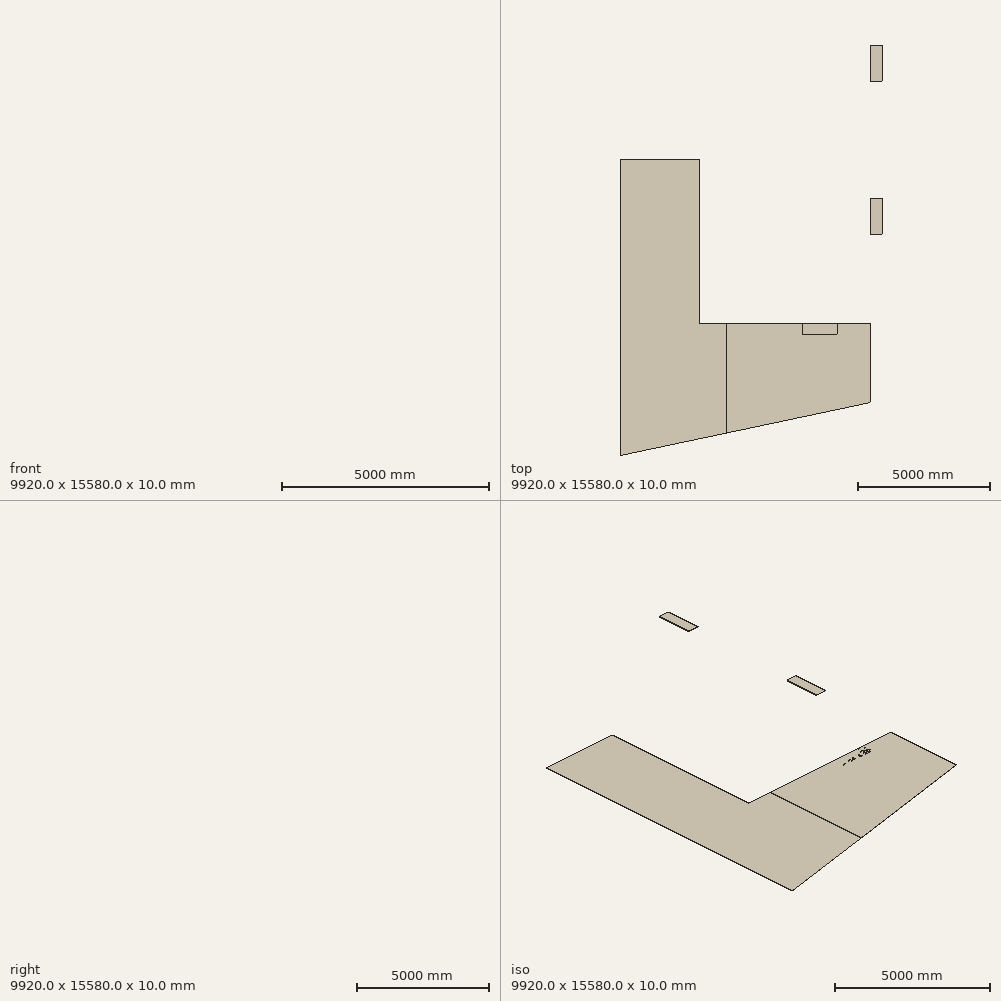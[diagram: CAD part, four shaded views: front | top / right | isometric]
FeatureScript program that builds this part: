
annotation { "Feature Type Name" : "Feature", "Feature Type Description" : "" }
export const myFeature = defineFeature(function(context is Context, id is Id, definition is map)
    precondition{}
    {
        {
            var Q0;
            Q0=qCreatedBy(makeId("Top.planeOp"),FACE);
            var sketch = newSketch(context, id + "F0", { "sketchPlane" : qUnion([Q0])});
            skLineSegment(sketch, "E0", {"start": v(0, 0) * mm, "end": v(14150, 3000) * mm});
            skLineSegment(sketch, "E1", {"start": v(14150, 3000) * mm, "end": v(14150, 27420) * mm});
            skLineSegment(sketch, "E2", {"start": v(14150, 27420) * mm, "end": v(0, 25000) * mm});
            skLineSegment(sketch, "E3", {"start": v(0, 25000) * mm, "end": v(0, 0) * mm});
            skSolve(sketch);
        }
        {
            var Q0;
            Q0=qCreatedBy(makeId("Top.planeOp"),FACE);
            var sketch = newSketch(context, id + "F1", { "sketchPlane" : qUnion([Q0])});
            skLineSegment(sketch, "E4.bottom", {"start": v(3000, 18250) * mm, "end": v(9500, 18250) * mm});
            skLineSegment(sketch, "E4.top", {"start": v(3000, 5000) * mm, "end": v(9500, 5000) * mm});
            skLineSegment(sketch, "E4.left", {"start": v(3000, 18250) * mm, "end": v(3000, 5000) * mm});
            skLineSegment(sketch, "E4.right", {"start": v(9500, 18250) * mm, "end": v(9500, 5000) * mm});
            skSolve(sketch);
        }
        {
            var Q0;
            Q0=qCreatedBy(makeId("Top.planeOp"),FACE);
            var sketch = newSketch(context, id + "F2", { "sketchPlane" : qUnion([Q0])});
            skLineSegment(sketch, "E5.bottom", {"start": v(3000, 11250) * mm, "end": v(0, 11250) * mm});
            skLineSegment(sketch, "E5.top", {"start": v(3000, 17250) * mm, "end": v(0, 17250) * mm});
            skLineSegment(sketch, "E5.left", {"start": v(3000, 11250) * mm, "end": v(3000, 17250) * mm});
            skLineSegment(sketch, "E5.right", {"start": v(0, 11250) * mm, "end": v(0, 17250) * mm});
            skSolve(sketch);
        }
        {
            var Q0;
            Q0=qCreatedBy(makeId("Top.planeOp"),FACE);
            var sketch = newSketch(context, id + "F3", { "sketchPlane" : qUnion([Q0])});
            skLineSegment(sketch, "E6", {"start": v(0, 11250) * mm, "end": v(3000, 11250) * mm});
            skLineSegment(sketch, "E7", {"start": v(3000, 11250) * mm, "end": v(3000, 5000) * mm});
            skLineSegment(sketch, "E8", {"start": v(3000, 5000) * mm, "end": v(4000, 5000) * mm});
            skLineSegment(sketch, "E9", {"start": v(4000, 5000) * mm, "end": v(4000, 848.06) * mm});
            skLineSegment(sketch, "E10", {"start": v(4000, 848.06) * mm, "end": v(0, 0) * mm});
            skLineSegment(sketch, "E11", {"start": v(0, 0) * mm, "end": v(0, 11250) * mm});
            skSolve(sketch);
        }
        {
            var Q0;
            Q0=qCreatedBy(makeId("Top.planeOp"),FACE);
            var sketch = newSketch(context, id + "F4", { "sketchPlane" : qUnion([Q0])});
            skLineSegment(sketch, "E12", {"start": v(4000, 4500) * mm, "end": v(10000, 4500) * mm});
            skLineSegment(sketch, "E13", {"start": v(10000, 4500) * mm, "end": v(10000, 18250) * mm});
            skLineSegment(sketch, "E14", {"start": v(10000, 18250) * mm, "end": v(9500, 18250) * mm});
            skLineSegment(sketch, "E15", {"start": v(9500, 18250) * mm, "end": v(9500, 5000) * mm});
            skLineSegment(sketch, "E16", {"start": v(9500, 5000) * mm, "end": v(4000, 5000) * mm});
            skLineSegment(sketch, "E17", {"start": v(4000, 5000) * mm, "end": v(4000, 4500) * mm});
            skSolve(sketch);
        }
        {
            var Q0;
            Q0=qCreatedBy(makeId("Top.planeOp"),FACE);
            var sketch = newSketch(context, id + "F5", { "sketchPlane" : qUnion([Q0])});
            skLineSegment(sketch, "E18.bottom", {"start": v(6880, 5000) * mm, "end": v(8230, 5000) * mm});
            skLineSegment(sketch, "E18.top", {"start": v(6880, 4580) * mm, "end": v(8230, 4580) * mm});
            skLineSegment(sketch, "E18.left", {"start": v(6880, 5000) * mm, "end": v(6880, 4580) * mm});
            skLineSegment(sketch, "E18.right", {"start": v(8230, 5000) * mm, "end": v(8230, 4580) * mm});
            skLineSegment(sketch, "E19.bottom", {"start": v(9500, 9750) * mm, "end": v(9920, 9750) * mm});
            skLineSegment(sketch, "E19.top", {"start": v(9500, 8400) * mm, "end": v(9920, 8400) * mm});
            skLineSegment(sketch, "E19.left", {"start": v(9500, 9750) * mm, "end": v(9500, 8400) * mm});
            skLineSegment(sketch, "E19.right", {"start": v(9920, 9750) * mm, "end": v(9920, 8400) * mm});
            skLineSegment(sketch, "E20.bottom", {"start": v(9500, 15580) * mm, "end": v(9920, 15580) * mm});
            skLineSegment(sketch, "E20.top", {"start": v(9500, 14230) * mm, "end": v(9920, 14230) * mm});
            skLineSegment(sketch, "E20.left", {"start": v(9500, 15580) * mm, "end": v(9500, 14230) * mm});
            skLineSegment(sketch, "E20.right", {"start": v(9920, 15580) * mm, "end": v(9920, 14230) * mm});
            skSolve(sketch);
        }
        {
            var Q0;
            Q0 = qSketchRegion(id + "F3", true);
            extrude(context, id + "F6", {"entities" : qUnion([Q0]), "oppositeDirection" : true, "depth" : 1 * mm, "offsetDistance" : 25 * mm});
        }
        {
            var Q0;
            Q0=qCreatedBy(makeId("Top.planeOp"),FACE);
            var sketch = newSketch(context, id + "F7", { "sketchPlane" : qUnion([Q0])});
            skLineSegment(sketch, "E21", {"start": v(4000, 848.06) * mm, "end": v(4000, 5000) * mm});
            skLineSegment(sketch, "E22", {"start": v(4000, 5000) * mm, "end": v(9500, 5000) * mm});
            skLineSegment(sketch, "E23", {"start": v(9500, 5000) * mm, "end": v(9500, 2014.13) * mm});
            skLineSegment(sketch, "E24", {"start": v(9500, 2014.13) * mm, "end": v(4000, 848.06) * mm});
            skSolve(sketch);
        }
        {
            var Q0;
            Q0 = qSketchRegion(id + "F7", true);
            extrude(context, id + "F8", {"entities" : qUnion([Q0]), "oppositeDirection" : true, "depth" : 10 * mm, "offsetDistance" : 25 * mm});
        }
        {
            var Q0;
            Q0 = qSketchRegion(id + "F5", true);
            extrude(context, id + "F9", {"entities" : qUnion([Q0]), "oppositeDirection" : true, "depth" : 10 * mm, "offsetDistance" : 25 * mm});
        }
    });
